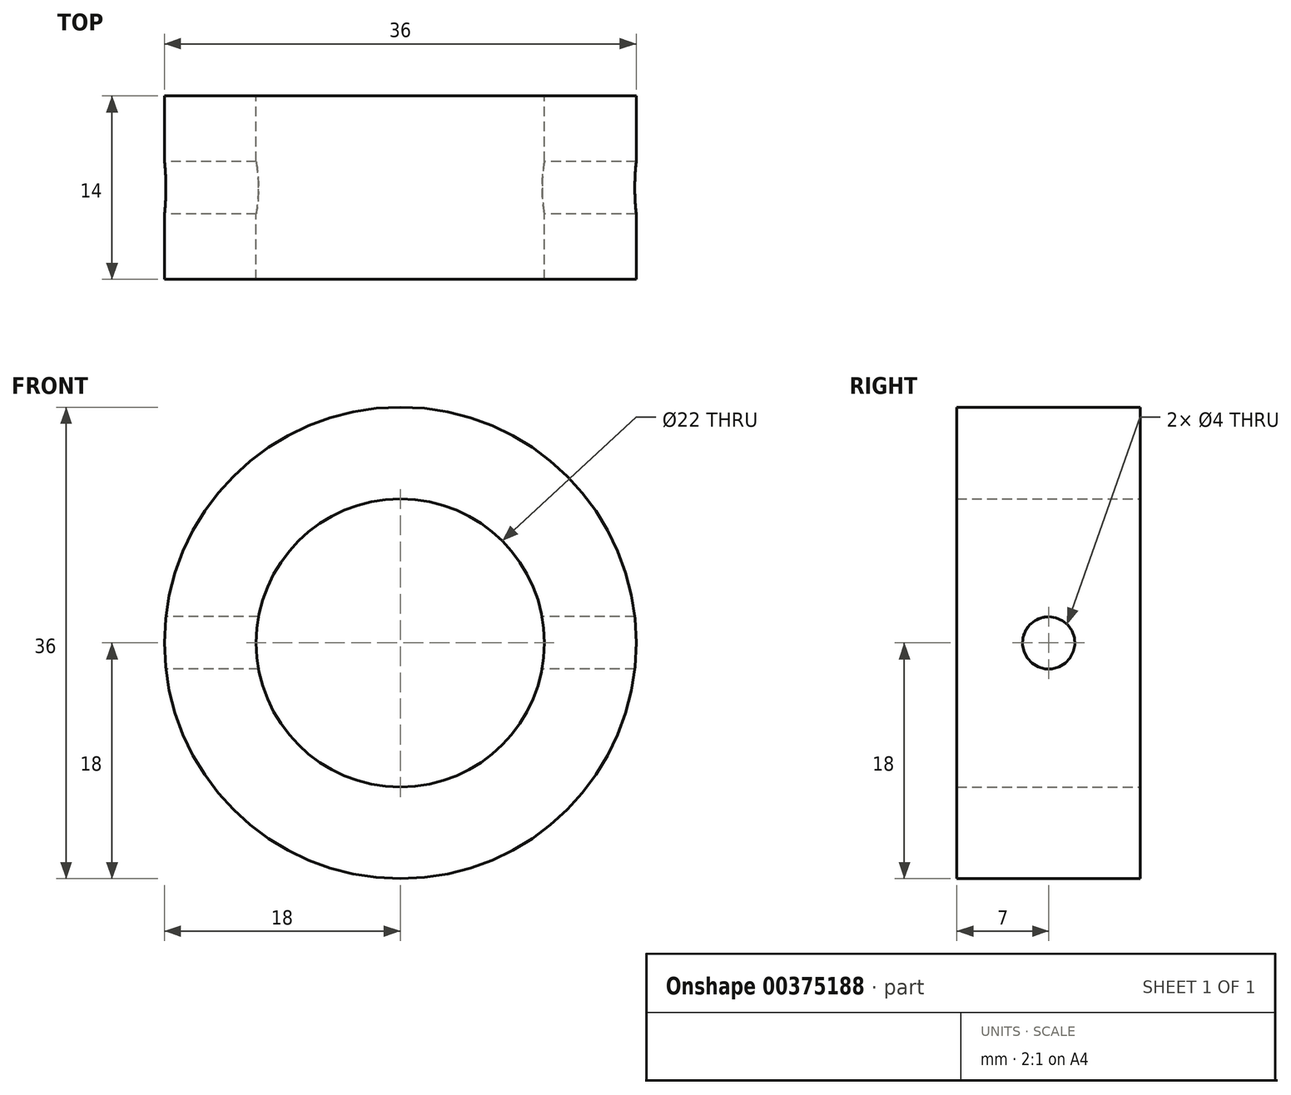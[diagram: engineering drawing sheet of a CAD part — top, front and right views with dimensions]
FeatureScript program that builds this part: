
annotation { "Feature Type Name" : "Feature", "Feature Type Description" : "" }
export const myFeature = defineFeature(function(context is Context, id is Id, definition is map)
    precondition{}
    {
        {
            var Q0;
            Q0=qCreatedBy(makeId("Front.planeOp"),FACE);
            var sketch = newSketch(context, id + "F0", { "sketchPlane" : qUnion([Q0])});
            skCircle(sketch, "E0", {"center": v(0, 0) * mm, "radius": 11 * mm});
            skCircle(sketch, "E1", {"center": v(0, 0) * mm, "radius": 18 * mm});
            skSolve(sketch);
        }
        {
            var Q0;
            Q0=makeQuery(id+"F0.imprint","IMPRINT",FACE,{"disambiguationData":[TD([[makeQuery(id+"F0.imprint","IMPRINT",EDGE,{"derivedFrom":sQuery(id+"F0.wireOp",EDGE,"E0")}),-1.0]])]});
            extrude(context, id + "F1", {"entities" : qUnion([Q0]), "depth" : 14 * mm, "symmetric" : true});
        }
        {
            var Q0;
            Q0=qCreatedBy(makeId("Right.planeOp"),FACE);
            var sketch = newSketch(context, id + "F2", { "sketchPlane" : qUnion([Q0])});
            skCircle(sketch, "E2", {"center": v(0, 0) * mm, "radius": 2 * mm});
            skSolve(sketch);
        }
        {
            var Q0;
            Q0 = qSketchRegion(id + "F2", true);
            extrude(context, id + "F3", {"entities" : qUnion([Q0]), "operationType" : NewBodyOperationType.REMOVE, "depth" : 69.6 * mm, "symmetric" : true});
        }
    });
